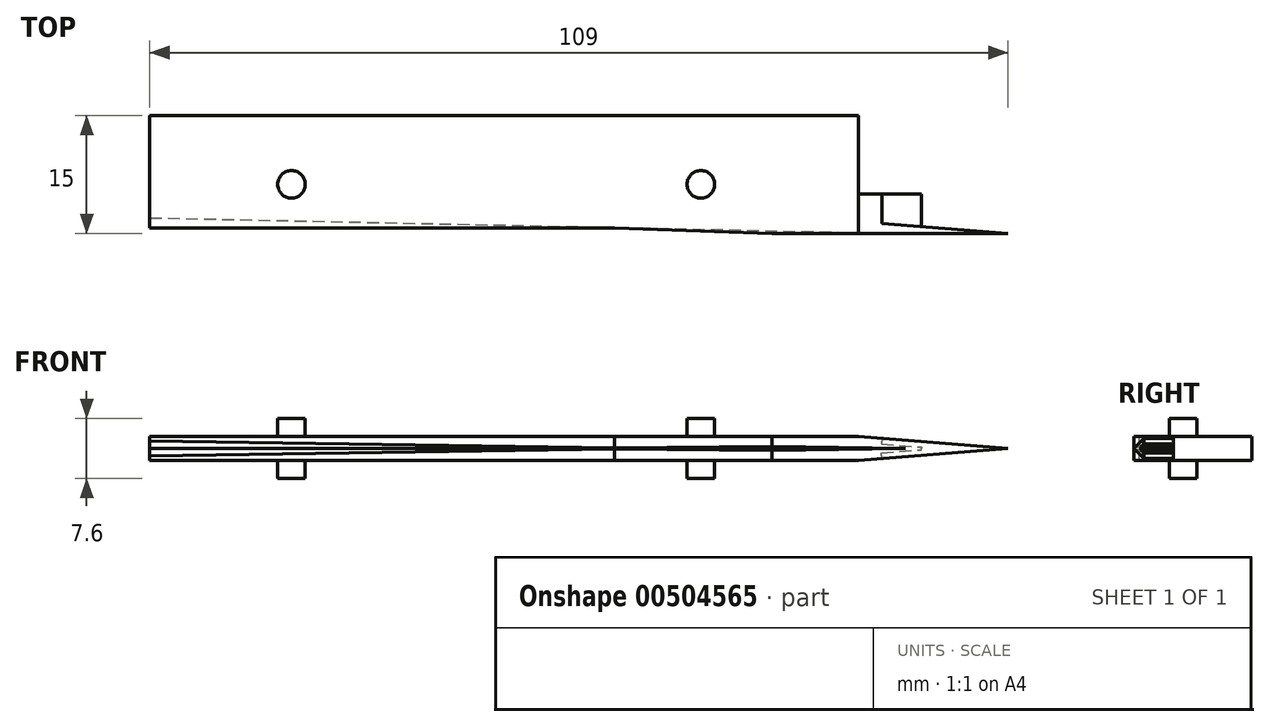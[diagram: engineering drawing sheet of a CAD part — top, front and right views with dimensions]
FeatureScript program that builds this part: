
annotation { "Feature Type Name" : "Feature", "Feature Type Description" : "" }
export const myFeature = defineFeature(function(context is Context, id is Id, definition is map)
    precondition{}
    {
        {
            var Q0;
            Q0=qCreatedBy(makeId("Front.planeOp"),FACE);
            var sketch = newSketch(context, id + "F0", { "sketchPlane" : qUnion([Q0])});
            skLineSegment(sketch, "E0", {"start": v(0, -1.5) * mm, "end": v(19, 0) * mm});
            skLineSegment(sketch, "E1", {"start": v(0, 0) * mm, "end": v(0, -1.5) * mm});
            skLineSegment(sketch, "E2", {"start": v(0, 0) * mm, "end": v(19, 0) * mm});
            skLineSegment(sketch, "E3.MirrorCS", {"start": v(0, 1.5) * mm, "end": v(19, 0) * mm});
            skLineSegment(sketch, "E4.MirrorCS", {"start": v(0, 0) * mm, "end": v(0, 1.5) * mm});
            skLineSegment(sketch, "E5", {"start": v(0, -0.8) * mm, "end": v(10.13, 0) * mm});
            skLineSegment(sketch, "E6.MirrorCS", {"start": v(0, 0.8) * mm, "end": v(10.13, 0) * mm});
            skLineSegment(sketch, "E7", {"start": v(8, -0.17) * mm, "end": v(7.99, 0) * mm});
            skLineSegment(sketch, "E8.MirrorCS", {"start": v(8, 0.17) * mm, "end": v(7.99, 0) * mm});
            skLineSegment(sketch, "E9", {"start": v(3, -1.26) * mm, "end": v(2.95, -0.57) * mm});
            skLineSegment(sketch, "E10.MirrorCS", {"start": v(3, 1.26) * mm, "end": v(2.95, 0.57) * mm});
            skSolve(sketch);
        }
        {
            var Q0;
            Q0 = qSketchRegion(id + "F0", true);
            var Q1;
            {var subQ3=sQuery(id+"F0.wireOp",EDGE,"E7");Q1=makeQuery(id+"F0.imprint","IMPRINT",FACE,{"disambiguationData":[TD([[makeQuery(id+"F0.imprint","IMPRINT",EDGE,{"derivedFrom":subQ3}),-1.0]])]});}
            var Q2;
            {var subQ3=sQuery(id+"F0.wireOp",EDGE,"E8.MirrorCS");Q2=makeQuery(id+"F0.imprint","IMPRINT",FACE,{"disambiguationData":[TD([[makeQuery(id+"F0.imprint","IMPRINT",EDGE,{"derivedFrom":subQ3}),1.0]])]});}
            extrude(context, id + "F1", {"entities" : qUnion([Q0, Q1, Q2]), "oppositeDirection" : true, "depth" : 1.5 * mm});
        }
        {
            var Q0;
            Q0=makeQuery(id+"F1.opExtrude","SWEPT_FACE",FACE,{"disambiguationData":[OSD([sQuery(id+"F0.wireOp",EDGE,"E3.MirrorCS")])]});
            var sketch = newSketch(context, id + "F2", { "sketchPlane" : qUnion([Q0])});
            skLineSegment(sketch, "E11", {"start": v(-0.12, 1.5) * mm, "end": v(18.94, 0) * mm});
            skSolve(sketch);
        }
        {
            var Q0;
            Q0=makeQuery(id+"F2.imprint","IMPRINT",FACE,{"disambiguationData":[TD([[makeQuery(id+"F2.imprint","IMPRINT",EDGE,{"derivedFrom":sQuery(id+"F2.wireOp",EDGE,"E11")}),1.0]])]});
            extrude(context, id + "F3", {"entities" : qUnion([Q0]), "operationType" : NewBodyOperationType.REMOVE, "oppositeDirection" : true, "depth" : 25 * mm});
        }
        {
            var Q0;
            {var subQ3=sQuery(id+"F0.wireOp",EDGE,"E8.MirrorCS");Q0=makeQuery(id+"F0.imprint","IMPRINT",FACE,{"disambiguationData":[TD([[makeQuery(id+"F0.imprint","IMPRINT",EDGE,{"derivedFrom":subQ3}),-1.0]])]});}
            var Q1;
            {var subQ5=sQuery(id+"F0.wireOp",EDGE,"E7");Q1=makeQuery(id+"F0.imprint","IMPRINT",FACE,{"disambiguationData":[TD([[makeQuery(id+"F0.imprint","IMPRINT",EDGE,{"derivedFrom":subQ5}),1.0]])]});}
            var Q2;
            {var subQ3=sQuery(id+"F0.wireOp",EDGE,"E9");Q2=makeQuery(id+"F0.imprint","IMPRINT",FACE,{"disambiguationData":[TD([[makeQuery(id+"F0.imprint","IMPRINT",EDGE,{"derivedFrom":subQ3}),1.0]])]});}
            var Q3;
            {var subQ3=sQuery(id+"F0.wireOp",EDGE,"E10.MirrorCS");Q3=makeQuery(id+"F0.imprint","IMPRINT",FACE,{"disambiguationData":[TD([[makeQuery(id+"F0.imprint","IMPRINT",EDGE,{"derivedFrom":subQ3}),-1.0]])]});}
            extrude(context, id + "F4", {"entities" : qUnion([Q0, Q1, Q2, Q3]), "operationType" : NewBodyOperationType.ADD, "oppositeDirection" : true, "depth" : 5 * mm});
        }
        {
            var Q0;
            Q0=qCreatedBy(makeId("Top.planeOp"),FACE);
            var sketch = newSketch(context, id + "F5", { "sketchPlane" : qUnion([Q0])});
            skCircle(sketch, "E12", {"center": v(-20, 6.25) * mm, "radius": 1.75 * mm});
            skCircle(sketch, "E13", {"center": v(-72, 6.25) * mm, "radius": 1.75 * mm});
            skSolve(sketch);
        }
        {
            var Q0;
            Q0=makeQuery(id+"F1.opExtrude","CAP_FACE",FACE,{"disambiguationData":[OSD([sQuery(id+"F0.wireOp",EDGE,"E0"),sQuery(id+"F0.wireOp",EDGE,"E1"),sQuery(id+"F0.wireOp",EDGE,"E3.MirrorCS"),sQuery(id+"F0.wireOp",EDGE,"E4.MirrorCS")])],"isStart":true});
            var sketch = newSketch(context, id + "F6", { "sketchPlane" : qUnion([Q0])});
            skLineSegment(sketch, "E14.bottom", {"start": v(0, -1.5) * mm, "end": v(-90, -1.5) * mm});
            skLineSegment(sketch, "E14.top", {"start": v(0, 1.5) * mm, "end": v(-90, 1.5) * mm});
            skLineSegment(sketch, "E14.left", {"start": v(0, -1.5) * mm, "end": v(0, 1.5) * mm});
            skLineSegment(sketch, "E14.right", {"start": v(-90, -1.5) * mm, "end": v(-90, 1.5) * mm});
            skSolve(sketch);
        }
        {
            var Q0;
            Q0=makeQuery(id+"F6.imprint","IMPRINT",FACE,{"disambiguationData":[TD([[makeQuery(id+"F6.imprint","IMPRINT",EDGE,{"derivedFrom":sQuery(id+"F6.wireOp",EDGE,"E14.bottom")}),-1.0]])]});
            var Q1;
            Q1=makeQuery(id+"F4.opExtrude","CAP_FACE",FACE,{"disambiguationData":[OSD([sQuery(id+"F0.wireOp",EDGE,"E0"),sQuery(id+"F0.wireOp",EDGE,"E1"),sQuery(id+"F0.wireOp",EDGE,"E3.MirrorCS"),sQuery(id+"F0.wireOp",EDGE,"E4.MirrorCS"),sQuery(id+"F0.wireOp",EDGE,"E5"),sQuery(id+"F0.wireOp",EDGE,"E6.MirrorCS"),sQuery(id+"F0.wireOp",EDGE,"E7"),sQuery(id+"F0.wireOp",EDGE,"E8.MirrorCS"),sQuery(id+"F0.wireOp",EDGE,"E9"),sQuery(id+"F0.wireOp",EDGE,"E10.MirrorCS")])],"isStart":false});
            extrude(context, id + "F7", {"entities" : qUnion([Q0]), "operationType" : NewBodyOperationType.ADD, "endBound" : BoundingType.UP_TO_SURFACE, "oppositeDirection" : true, "endBoundEntityFace" : qUnion([Q1]), "depth" : 25 * mm});
        }
        {
            var Q0;
            Q0=makeQuery(id+"F5.imprint","IMPRINT",FACE,{"disambiguationData":[TD([[makeQuery(id+"F5.imprint","IMPRINT",EDGE,{"derivedFrom":sQuery(id+"F5.wireOp",EDGE,"E12")}),1.0]])]});
            var Q1;
            Q1=makeQuery(id+"F5.imprint","IMPRINT",FACE,{"disambiguationData":[TD([[makeQuery(id+"F5.imprint","IMPRINT",EDGE,{"derivedFrom":sQuery(id+"F5.wireOp",EDGE,"E13")}),1.0]])]});
            extrude(context, id + "F8", {"entities" : qUnion([Q0, Q1]), "operationType" : NewBodyOperationType.ADD, "endBound" : BoundingType.SYMMETRIC, "depth" : 7.6 * mm});
        }
        {
            var Q0;
            {var subQ0=sQuery(id+"F0.wireOp",EDGE,"E10.MirrorCS");var subQ1=sQuery(id+"F0.wireOp",EDGE,"E9");var subQ2=sQuery(id+"F0.wireOp",EDGE,"E8.MirrorCS");var subQ3=sQuery(id+"F0.wireOp",EDGE,"E7");var subQ4=sQuery(id+"F0.wireOp",EDGE,"E6.MirrorCS");var subQ5=sQuery(id+"F0.wireOp",EDGE,"E5");var subQ6=sQuery(id+"F0.wireOp",EDGE,"E4.MirrorCS");var subQ7=sQuery(id+"F0.wireOp",EDGE,"E3.MirrorCS");var subQ8=sQuery(id+"F0.wireOp",EDGE,"E1");var subQ9=sQuery(id+"F0.wireOp",EDGE,"E0");Q0=makeQuery(id+"F7.boolean.opBoolean","MERGE",FACE,{"derivedFrom":[makeQuery(id+"F4.opExtrude","CAP_FACE",FACE,{"disambiguationData":[OSD([subQ9,subQ8,subQ7,subQ6,subQ5,subQ4,subQ3,subQ2,subQ1,subQ0])],"isStart":false}),makeQuery(id+"F7.opExtrude","CAP_FACE",FACE,{"disambiguationData":[OSD([subQ9,subQ8,subQ7,subQ6,subQ5,subQ4,subQ3,subQ2,subQ1,subQ0])],"isStart":false})]});}
            var sketch = newSketch(context, id + "F9", { "sketchPlane" : qUnion([Q0])});
            skLineSegment(sketch, "E15.bottom", {"start": v(90, -1.5) * mm, "end": v(0, -1.5) * mm});
            skLineSegment(sketch, "E15.top", {"start": v(90, 1.5) * mm, "end": v(0, 1.5) * mm});
            skLineSegment(sketch, "E15.left", {"start": v(90, -1.5) * mm, "end": v(90, 1.5) * mm});
            skLineSegment(sketch, "E15.right", {"start": v(0, -1.5) * mm, "end": v(0, 1.5) * mm});
            skSolve(sketch);
        }
        {
            var Q0;
            Q0=makeQuery(id+"F9.imprint","IMPRINT",FACE,{"disambiguationData":[TD([[makeQuery(id+"F9.imprint","IMPRINT",EDGE,{"derivedFrom":sQuery(id+"F9.wireOp",EDGE,"E15.bottom")}),-1.0]])]});
            extrude(context, id + "F10", {"entities" : qUnion([Q0]), "operationType" : NewBodyOperationType.ADD, "depth" : 10 * mm});
        }
        {
            var Q0;
            Q0=qCreatedBy(makeId("Top.planeOp"),FACE);
            var sketch = newSketch(context, id + "F11", { "sketchPlane" : qUnion([Q0])});
            skLineSegment(sketch, "E16", {"start": v(-90, 2) * mm, "end": v(6, 0) * mm});
            skSolve(sketch);
        }
        {
            var Q0;
            Q0=makeQuery(id+"F10.boolean.opBoolean","MERGE",FACE,{"derivedFrom":[makeQuery(id+"F7.opExtrude","SWEPT_FACE",FACE,{"disambiguationData":[OSD([sQuery(id+"F6.wireOp",EDGE,"E14.right")])]}),makeQuery(id+"F10.opExtrude","SWEPT_FACE",FACE,{"disambiguationData":[OSD([sQuery(id+"F9.wireOp",EDGE,"E15.left")])]})]});
            var sketch = newSketch(context, id + "F12", { "sketchPlane" : qUnion([Q0])});
            skLineSegment(sketch, "E17", {"start": v(0, -1.5) * mm, "end": v(-2, 0) * mm});
            skLineSegment(sketch, "E18", {"start": v(-2, 0) * mm, "end": v(0, 1.5) * mm});
            skLineSegment(sketch, "E19", {"start": v(0, 1.5) * mm, "end": v(0, -1.5) * mm});
            skSolve(sketch);
        }
        {
            var Q0;
            Q0=makeQuery(id+"F12.imprint","IMPRINT",FACE,{"disambiguationData":[TD([[makeQuery(id+"F12.imprint","IMPRINT",EDGE,{"derivedFrom":sQuery(id+"F12.wireOp",EDGE,"E17")}),-1.0]])]});
            var Q1;
            Q1=sQuery(id+"F11.wireOp",EDGE,"E16");
            sweep(context, id + "F13", {"operationType" : NewBodyOperationType.REMOVE, "profiles" : qUnion([Q0]), "path" : qUnion([Q1])});
        }
        {
            var Q0;
            Q0=makeQuery(id+"F10.boolean.opBoolean","MERGE",FACE,{"derivedFrom":[makeQuery(id+"F7.opExtrude","SWEPT_FACE",FACE,{"disambiguationData":[OSD([sQuery(id+"F6.wireOp",EDGE,"E14.top")])]}),makeQuery(id+"F10.opExtrude","SWEPT_FACE",FACE,{"disambiguationData":[OSD([sQuery(id+"F9.wireOp",EDGE,"E15.top")])]})]});
            var sketch = newSketch(context, id + "F14", { "sketchPlane" : qUnion([Q0])});
            skLineSegment(sketch, "E20", {"start": v(-90, 0) * mm, "end": v(-90, 0.7) * mm});
            skLineSegment(sketch, "E21", {"start": v(-90, 0.7) * mm, "end": v(-31, 0.7) * mm});
            skLineSegment(sketch, "E22", {"start": v(-31, 0.7) * mm, "end": v(-10.95, 0) * mm});
            skLineSegment(sketch, "E23", {"start": v(-10.95, 0) * mm, "end": v(-90, 0) * mm});
            skSolve(sketch);
        }
        {
            var Q0;
            Q0=makeQuery(id+"F14.imprint","IMPRINT",FACE,{"disambiguationData":[TD([[makeQuery(id+"F14.imprint","IMPRINT",EDGE,{"derivedFrom":sQuery(id+"F14.wireOp",EDGE,"E20")}),1.0]])]});
            extrude(context, id + "F15", {"entities" : qUnion([Q0]), "operationType" : NewBodyOperationType.REMOVE, "endBound" : BoundingType.THROUGH_ALL, "oppositeDirection" : true, "depth" : 25 * mm});
        }
    });
